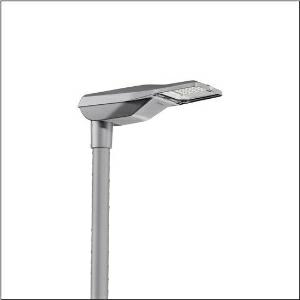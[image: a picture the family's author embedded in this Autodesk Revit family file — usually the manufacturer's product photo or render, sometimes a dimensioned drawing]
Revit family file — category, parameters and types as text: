
# Revit family: streetlight_sl_21_iq_micro___st0_8a_5xe1c21d08cb_82e6
name_source: partatom
category: Lighting Fixtures
units: mm (PartAtom-declared; Revit-internal decimal feet)

## family parameters
Cut with Voids When Loaded = No
Host = Face
Light Source = No
Part Type = Normal
Room Calculation Point = No
Round Connector Dimension = Use Diameter
Shared = No

## types (1)
- --- (1 x LED, 2380 lm, 19.4 W, 2200K)
    Apparent Load = 19 VA
    CIE Flux Codes = 38 75 97 100 100
    Color Rendering = 70
    Color Temperature = 2200K
    Default Elevation = 1800 mm
    Description = Streetlight SL 21 iQ micro, mast luminaire, primary light control with lens, of PMMA, primary optical cover: cover, of toughened safety glass, transparent, light distribution: ST0.8a, light emission: direct distribution, primary light characteristic: asymmetric, installation type: post-top, side-entry, LED, High Power LED, rated luminous flux: 2.380lm, luminous efficacy: 123lm/W, light colour: 722, colour temperature: 2200K, control gear: iQ-Comfort, control: Auto-Match, Temp-Guard, Lumen-Switch, Night-Set, Smart-Wire, Light-Fading, Desk-Remote (wireless, voltage-free reading and setting of iQ features in the workshop via application-optimized NFC function/RFID function), optimised constant luminous flux control (CLO 2.0), pre-setting: linear dimming characteristic, mains connection: 220..240V, AC, 50/60Hz, start of lifetime: 19W, end of service life: 20W, reduction: 10W, luminaire housing, of diecast aluminium, powder-coated, SITECO metallic grey (DB 702S), corrosivity category C5 high according to DIN EN ISO 12944, please order mast flange separately, inclination adjustable: 0°, 5°, 10°, 15°, sealing non-destructively replaceable, multi-level sealing system, length: 528mm, width: 235mm, height: 110mm, mast flange for spigot size: 42mm (side-entry): 5XC10008XM4, 60/48mm (side-entry/post-top): 5XC10108XM2, 76/60mm (side-entry/post-top): 5XC10108XM1, protection rating (complete): IP66, insulation class (complete): insulation class II (safety insulation), certification: CE, ENEC, ENEC+, VDE, impact resistance: IK10, permissible operating ambient temperature for outdoor applications: -40..+50°C, standard-compliant lighting for roads and squares, packaging unit: 1 piece

Light Distribution: ST0.8a
    Height = 110 mm
    Lamp = 1 x LED
    Lamp Light Flux = 2380 lm
    Lamp Power = 19.4 W
    Lamp count = 1
    Length = 528 mm
    Luminous efficacy = 123 lm/W
    Manufacturer = Siteco
    ModVariant = No
    Model = 5XE1C21D08CB
    Number of Poles = 1
    OnlyDefault = Yes
    Power Factor = 1
    Product Name = Streetlight SL 21 iQ micro | ST0.8a
    Product group = mast luminaire | pylon top
    ProductGroupID = 6100
    Protection Class = Protection class II
    Protection Degree = IP 66
    RLX_Detail_Level = 1
    RLX_Emergency_Light_Flux = 0 lm
    RLX_Emergency_Type = 0
    RLX_Emergency_Type_DB = No
    RlxData = <blob elided: 98493 chars, md5=51a3d60b>
    Socket = socket
    Standby Power = 0 W
    System Light Flux = 2380 lm
    System Power = 19 W
    Type Comments = factory setting: luminous flux: 100 % | dim-lin: 254 | 387 mA
    Type Image = l_1006881.jpg
    URL = http://relux.com
    VarID = @adj_138031
    Voltage = 0 V
    Weight = 0.00 kg
    Width = 235 mm

## geometry (parser evidence)
native form markers: Blend x4, Sweep x10
no freeform markers — native parametric forms only
